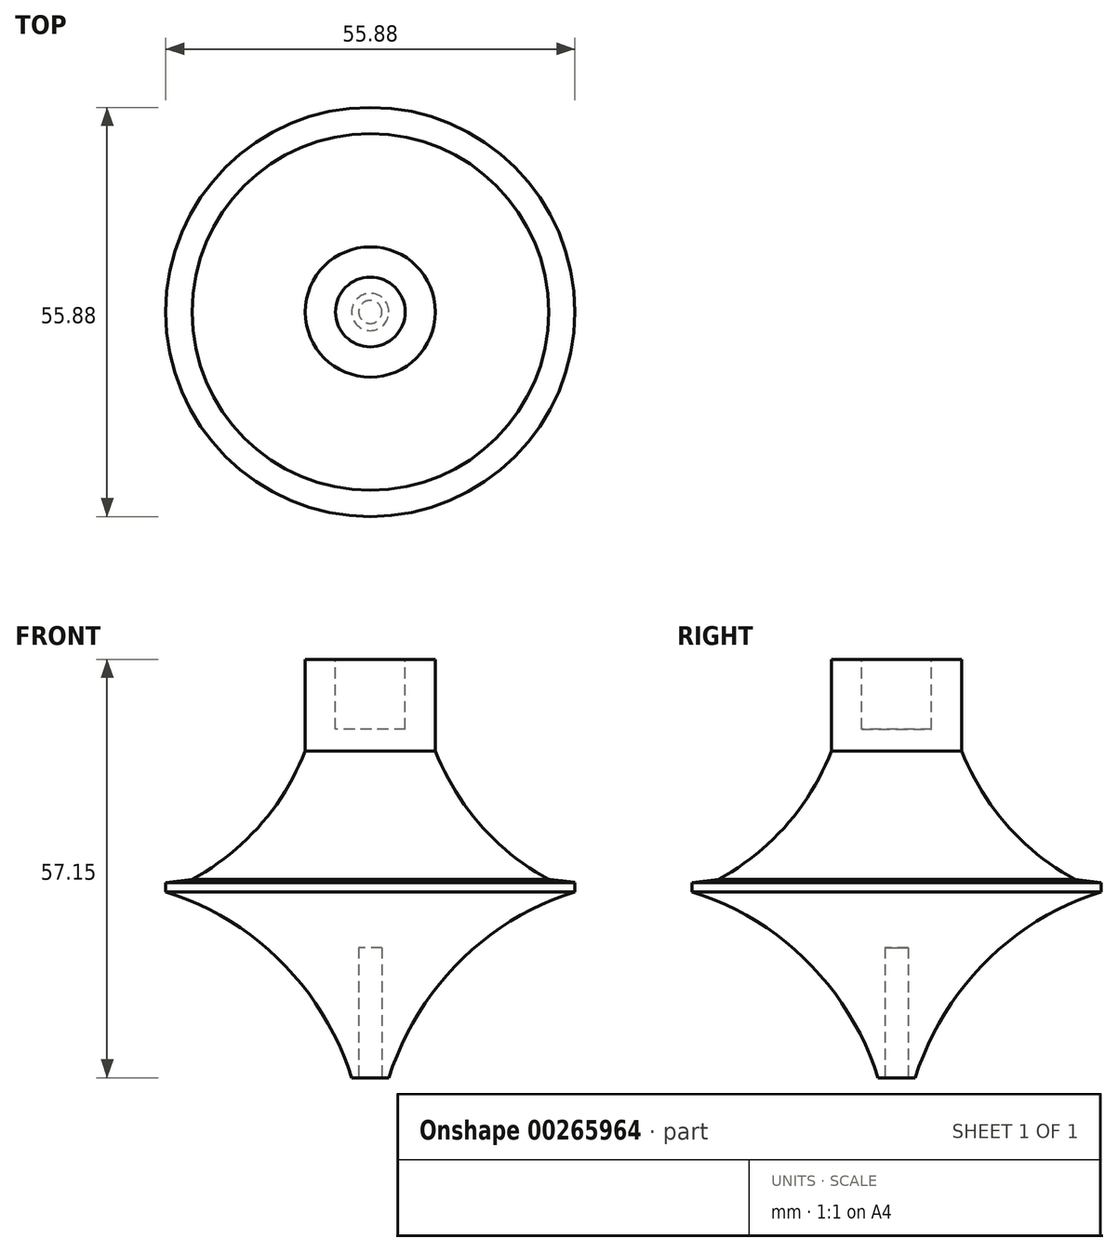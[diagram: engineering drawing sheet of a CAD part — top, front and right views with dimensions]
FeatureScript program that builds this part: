
annotation { "Feature Type Name" : "Feature", "Feature Type Description" : "" }
export const myFeature = defineFeature(function(context is Context, id is Id, definition is map)
    precondition{}
    {
        {
            var Q0;
            Q0=qCreatedBy(makeId("Front.planeOp"),FACE);
            var sketch = newSketch(context, id + "F0", { "sketchPlane" : qUnion([Q0])});
            skPoint(sketch, "E0", {"position": v(0, 31.75) * mm});
            skPoint(sketch, "E1", {"position": v(0, 57.15) * mm});
            skArc(sketch, "E2", {"start": v(27.94, 25.4) * mm, "mid": v(12.13, 15.8) * mm, "end": v(2.54, 0) * mm});
            skLineSegment(sketch, "E3", {"start": v(0, 57.15) * mm, "end": v(8.89, 57.15) * mm});
            skLineSegment(sketch, "E4", {"start": v(0, 57.15) * mm, "end": v(0, 0) * mm});
            skLineSegment(sketch, "E5", {"start": v(0, 0) * mm, "end": v(2.54, 0) * mm});
            skLineSegment(sketch, "E6", {"start": v(8.89, 57.15) * mm, "end": v(8.89, 44.64) * mm});
            skArc(sketch, "E7", {"start": v(8.89, 44.64) * mm, "mid": v(11.77, 38.9) * mm, "end": v(15.69, 33.8) * mm});
            skArc(sketch, "E8", {"start": v(15.69, 33.8) * mm, "mid": v(15.7, 33.78) * mm, "end": v(15.73, 33.76) * mm});
            skArc(sketch, "E9", {"start": v(15.73, 33.76) * mm, "mid": v(19.77, 30.07) * mm, "end": v(24.35, 27.08) * mm});
            skLineSegment(sketch, "E10", {"start": v(27.94, 25.4) * mm, "end": v(27.94, 26.67) * mm});
            skLineSegment(sketch, "E11", {"start": v(27.94, 26.67) * mm, "end": v(24.35, 27.08) * mm});
            skSolve(sketch);
        }
        {
            var Q0;
            Q0=makeQuery(id+"F0.imprint","IMPRINT",FACE,{"disambiguationData":[TD([[makeQuery(id+"F0.imprint","IMPRINT",EDGE,{"derivedFrom":sQuery(id+"F0.wireOp",EDGE,"E2")}),-1.0]])]});
            var Q1;
            Q1=sQuery(id+"F0.wireOp",EDGE,"E4");
            revolve(context, id + "F1", {"entities" : qUnion([Q0]), "axis" : qUnion([Q1]), "revolveType" : RevolveType.FULL});
        }
        {
            var Q0;
            Q0=qCreatedBy(makeId("Top.planeOp"),FACE);
            var sketch = newSketch(context, id + "F2", { "sketchPlane" : qUnion([Q0])});
            skCircle(sketch, "E12", {"center": v(0, 0) * mm, "radius": 1.59 * mm});
            skSolve(sketch);
        }
        {
            var Q0;
            Q0=makeQuery(id+"F1.opRevolve","SWEPT_FACE",FACE,{"disambiguationData":[OSD([sQuery(id+"F0.wireOp",EDGE,"E3")])]});
            var sketch = newSketch(context, id + "F3", { "sketchPlane" : qUnion([Q0])});
            skCircle(sketch, "E13", {"center": v(0, 0) * mm, "radius": 4.76 * mm});
            skSolve(sketch);
        }
        {
            var Q0;
            Q0 = qSketchRegion(id + "F2", true);
            var Q1;
            Q1=sQuery(id+"F2.wireOp",EDGE,"E12");
            extrude(context, id + "F4", {"entities" : qUnion([Q0]), "operationType" : NewBodyOperationType.REMOVE, "surfaceEntities" : qUnion([Q1]), "depth" : 17.78 * mm});
        }
        {
            var Q0;
            Q0=makeQuery(id+"F3.imprint","IMPRINT",FACE,{"disambiguationData":[TD([[makeQuery(id+"F3.imprint","IMPRINT",EDGE,{"derivedFrom":sQuery(id+"F3.wireOp",EDGE,"E13")}),1.0]])]});
            var Q1;
            Q1=sQuery(id+"F3.wireOp",EDGE,"E13");
            extrude(context, id + "F5", {"entities" : qUnion([Q0]), "operationType" : NewBodyOperationType.REMOVE, "surfaceEntities" : qUnion([Q1]), "oppositeDirection" : true, "depth" : 9.52 * mm});
        }
    });
